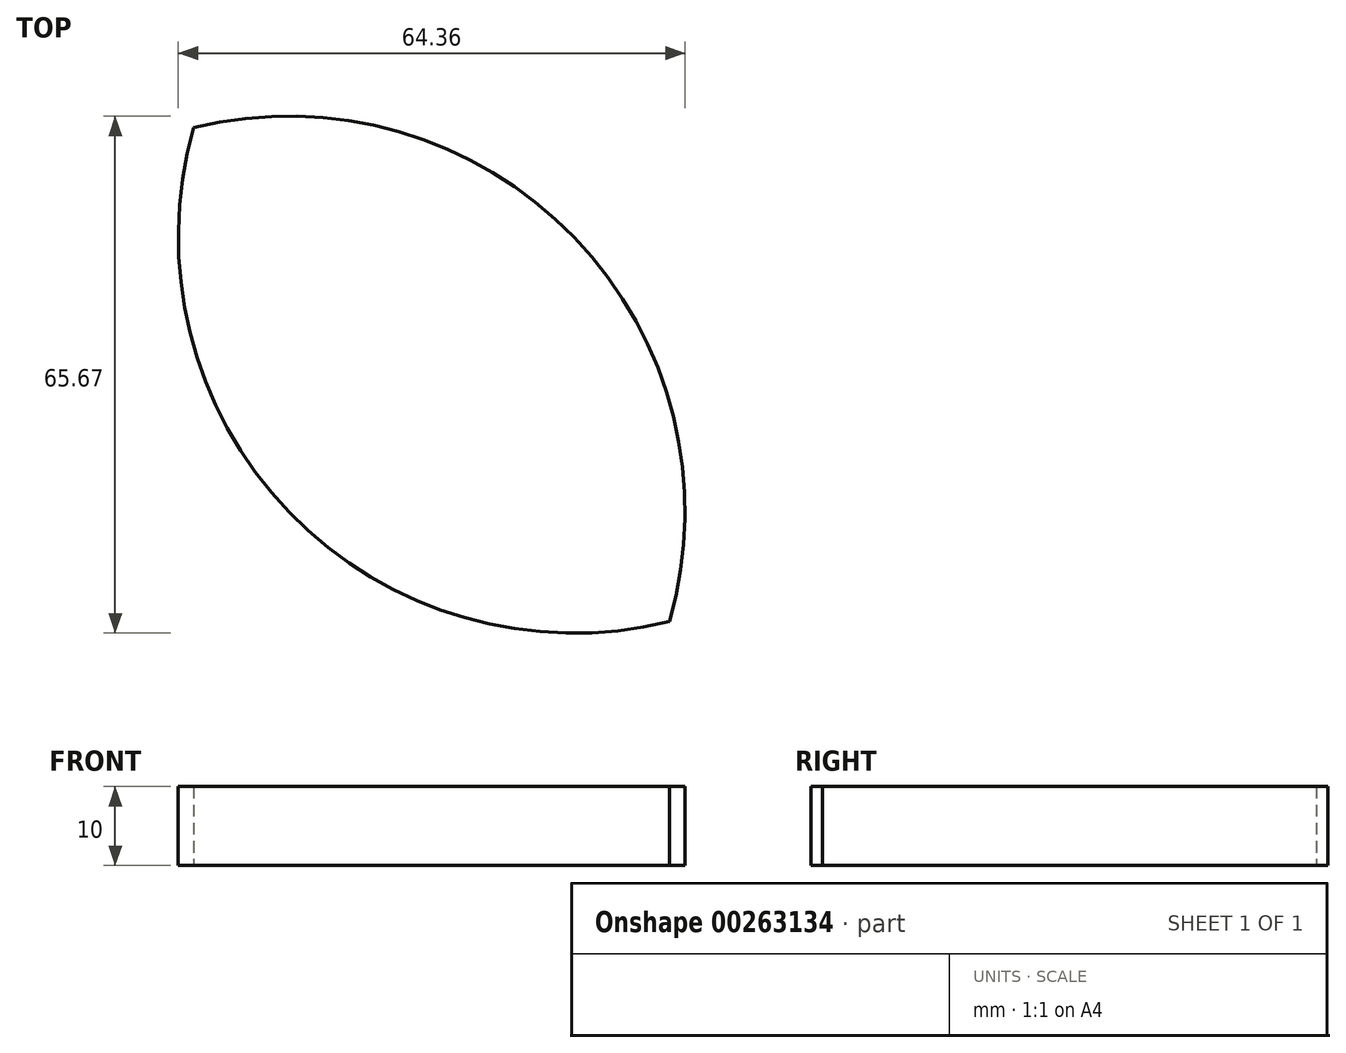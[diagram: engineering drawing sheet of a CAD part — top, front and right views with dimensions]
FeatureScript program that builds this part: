
annotation { "Feature Type Name" : "Feature", "Feature Type Description" : "" }
export const myFeature = defineFeature(function(context is Context, id is Id, definition is map)
    precondition{}
    {
        {
            var Q0;
            Q0=qCreatedBy(makeId("Top.planeOp"),FACE);
            var sketch = newSketch(context, id + "F0", { "sketchPlane" : qUnion([Q0])});
            skCircle(sketch, "E0", {"center": v(0, 0) * mm, "radius": 50.28 * mm});
            skCircle(sketch, "E1", {"center": v(36.2, 34.9) * mm, "radius": 50.28 * mm});
            skSolve(sketch);
        }
        {
            var Q0;
            {var subQ0=sQuery(id+"F0.wireOp",EDGE,"E1");var subQ1=sQuery(id+"F0.wireOp",EDGE,"E0");var subQ2=makeQuery(id+"F0.imprint","INTERSECT",VERTEX,{"disambiguationData":[OD(0.0)],"derivedFrom":[subQ1,subQ0]});Q0=makeQuery(id+"F0.imprint","IMPRINT",FACE,{"disambiguationData":[TD([[makeQuery(id+"F0.imprint","IMPRINT",EDGE,{"disambiguationData":[TD([[subQ2,1.0]])],"derivedFrom":subQ1}),1.0]])]});}
            extrude(context, id + "F1", {"entities" : qUnion([Q0]), "depth" : 10 * mm, "offsetDistance" : 25.4 * mm});
        }
    });
